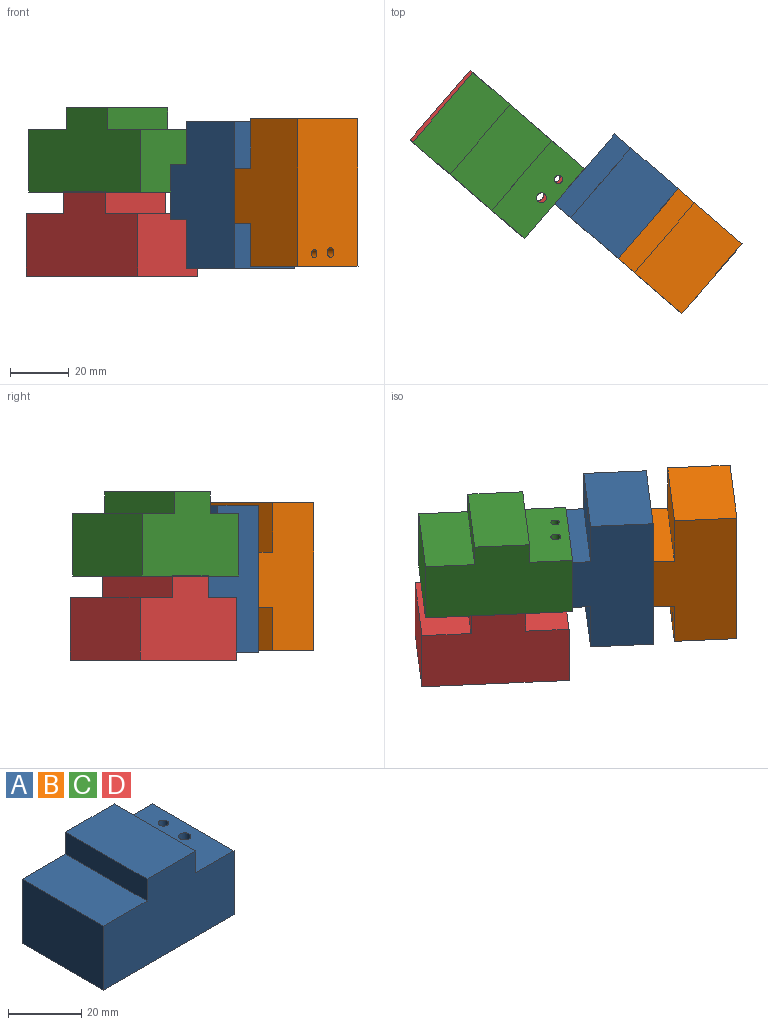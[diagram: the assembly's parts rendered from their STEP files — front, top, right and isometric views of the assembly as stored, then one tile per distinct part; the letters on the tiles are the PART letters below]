
ASSEMBLY  parts=4 mates=3
PART A: 12 faces, bbox 50.4x31.4x28.7 mm
  f0: plane 31.45x14.78mm, normal (0,0,1), area 449.4mm2, adj f1,f7,f8,f9,f10,f11
  f1: plane 31.45x7.33mm, normal (1,0,0), area 230.6mm2, adj f0,f2,f8,f9
  f2: plane 31.45x18.8mm, normal (0,0,1), area 591mm2, adj f1,f3,f8,f9
  f3: plane 31.45x7.33mm, normal (-1,0,0), area 230.6mm2, adj f2,f4,f8,f9
  f4: plane 31.45x16.85mm, normal (0,0,1), area 529.7mm2, adj f3,f5,f8,f9
  f5: plane 31.45x21.41mm, normal (-1,0,0), area 673.2mm2, adj f4,f6,f8,f9
  f6: plane 50.42x31.45mm, normal (0,0,-1), area 1570.2mm2, adj f5,f7,f8,f9,f10,f11
  f7: plane 31.45x21.41mm, normal (1,0,0), area 673.2mm2, adj f0,f6,f8,f9
  f8: plane 50.42x28.74mm, normal (0,1,0), area 1217.2mm2, adj f0,f1,f2,f3,f4,f5,f6,f7
  f9: plane 50.42x28.74mm, normal (0,-1,0), area 1217.2mm2, adj f0,f1,f2,f3,f4,f5,f6,f7
  f10: cylinder r=1.69mm len=21.41mm, axis (0,0,-1), area 226.8mm2, adj f0,f6
  f11: cylinder r=1.42mm len=21.41mm, axis (0,0,-1), area 191.1mm2, adj f0,f6
PART B: same geometry as A
PART C: same geometry as A
PART D: same geometry as A
PLACE A rot(axis=(-0.33,-0.89,-0.33),97deg) t=(-30.93,-1.63,33.55)mm
PLACE B rot(axis=(-0.68,0.25,0.68),151.5deg) t=(11.35,3.43,34.39)mm
PLACE C rot(axis=(0,0,-1),40.7deg) t=(-73.96,14.68,45.29)mm
PLACE D rot(axis=(0,0,-1),40.7deg) t=(-74.91,15.47,16.55)mm
MATE fastened B.f2 <-> A.f6  axis (-0.76,0.65,0) through (-12.57,3.28,33.35)mm
MATE revolute A.f2 <-> C.f7  axis (-0.76,0.65,0) through (-34.34,22.05,34.59)mm
MATE slider D.f2 <-> C.f6  axis (0,0,1) through (-63.87,26.7,34.59)mm
